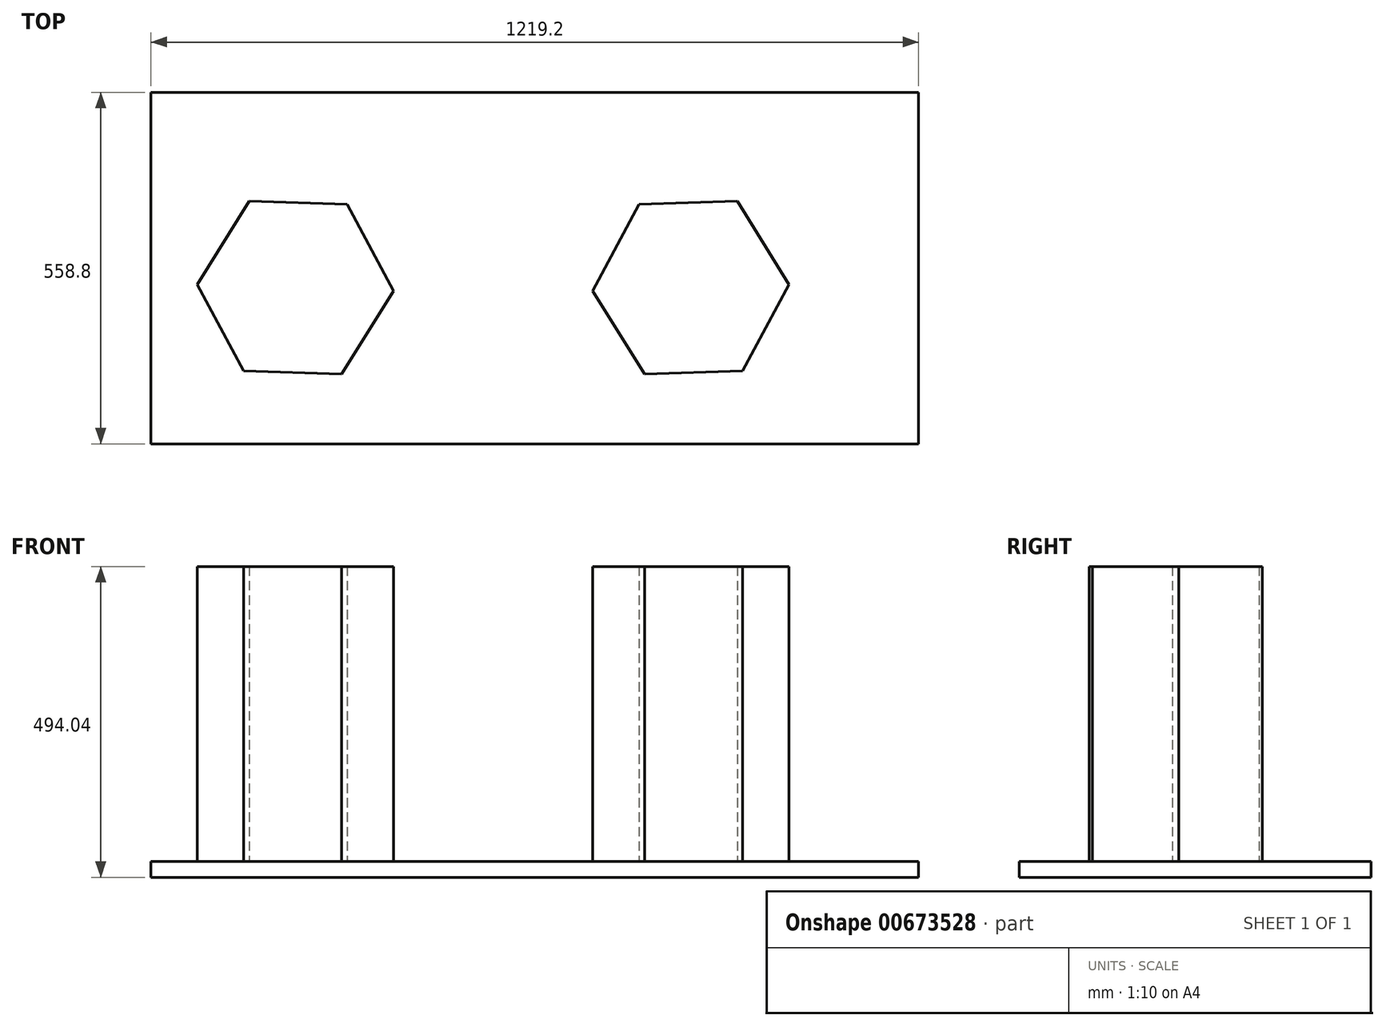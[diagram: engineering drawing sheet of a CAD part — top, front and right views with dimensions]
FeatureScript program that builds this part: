
annotation { "Feature Type Name" : "Feature", "Feature Type Description" : "" }
export const myFeature = defineFeature(function(context is Context, id is Id, definition is map)
    precondition{}
    {
        {
            var Q0;
            Q0=qCreatedBy(makeId("Top.planeOp"),FACE);
            var sketch = newSketch(context, id + "F0", { "sketchPlane" : qUnion([Q0])});
            skLineSegment(sketch, "E0.bottom", {"start": v(0, 0) * mm, "end": v(1219.2, 0) * mm});
            skLineSegment(sketch, "E0.top", {"start": v(0, 558.8) * mm, "end": v(1219.2, 558.8) * mm});
            skLineSegment(sketch, "E0.left", {"start": v(0, 0) * mm, "end": v(0, 558.8) * mm});
            skLineSegment(sketch, "E0.right", {"start": v(1219.2, 0) * mm, "end": v(1219.2, 558.8) * mm});
            skSolve(sketch);
        }
        {
            var Q0;
            Q0 = qSketchRegion(id + "F0", true);
            extrude(context, id + "F1", {"entities" : qUnion([Q0]), "oppositeDirection" : true, "depth" : 25.4 * mm, "offsetDistance" : 25.4 * mm});
        }
        {
            var Q0;
            Q0=makeQuery(id+"F1.opExtrude","CAP_FACE",FACE,{"disambiguationData":[OSD([sQuery(id+"F0.wireOp",EDGE,"E0.bottom"),sQuery(id+"F0.wireOp",EDGE,"E0.top"),sQuery(id+"F0.wireOp",EDGE,"E0.left"),sQuery(id+"F0.wireOp",EDGE,"E0.right")])],"isStart":true});
            var sketch = newSketch(context, id + "F2", { "sketchPlane" : qUnion([Q0])});
            skCircle(sketch, "E1.cCircle", {"center": v(229.23, 248.15) * mm, "radius": 155.97 * mm, "construction": true});
            skLineSegment(sketch, "E1.0", {"start": v(311.48, 380.67) * mm, "end": v(385.11, 243.18) * mm});
            skLineSegment(sketch, "E1.1", {"start": v(385.11, 243.18) * mm, "end": v(302.86, 110.66) * mm});
            skLineSegment(sketch, "E1.2", {"start": v(302.86, 110.66) * mm, "end": v(146.97, 115.64) * mm});
            skLineSegment(sketch, "E1.3", {"start": v(146.97, 115.64) * mm, "end": v(73.34, 253.13) * mm});
            skLineSegment(sketch, "E1.4", {"start": v(73.34, 253.13) * mm, "end": v(155.59, 385.64) * mm});
            skLineSegment(sketch, "E1.5", {"start": v(155.59, 385.64) * mm, "end": v(311.48, 380.67) * mm});
            skLineSegment(sketch, "E2", {"start": v(543.38, 98.5) * mm, "end": v(543.38, 453.78) * mm});
            skLineSegment(sketch, "E3.MirrorCS", {"start": v(701.65, 243.18) * mm, "end": v(783.9, 110.66) * mm});
            skCircle(sketch, "E4.MirrorC", {"center": v(857.53, 248.15) * mm, "radius": 155.97 * mm, "construction": true});
            skLineSegment(sketch, "E5.MirrorCS", {"start": v(783.9, 110.66) * mm, "end": v(939.78, 115.64) * mm});
            skLineSegment(sketch, "E6.MirrorCS", {"start": v(939.78, 115.64) * mm, "end": v(1013.42, 253.13) * mm});
            skLineSegment(sketch, "E7.MirrorCS", {"start": v(1013.42, 253.13) * mm, "end": v(931.17, 385.64) * mm});
            skLineSegment(sketch, "E8.MirrorCS", {"start": v(931.17, 385.64) * mm, "end": v(775.28, 380.67) * mm});
            skLineSegment(sketch, "E9.MirrorCS", {"start": v(775.28, 380.67) * mm, "end": v(701.65, 243.18) * mm});
            skSolve(sketch);
        }
        {
            var Q0;
            Q0=makeQuery(id+"F2.imprint","IMPRINT",FACE,{"disambiguationData":[TD([[makeQuery(id+"F2.imprint","IMPRINT",EDGE,{"derivedFrom":sQuery(id+"F2.wireOp",EDGE,"E1.0")}),-1.0]])]});
            var Q1;
            Q1=makeQuery(id+"F2.imprint","IMPRINT",FACE,{"disambiguationData":[TD([[makeQuery(id+"F2.imprint","IMPRINT",EDGE,{"derivedFrom":sQuery(id+"F2.wireOp",EDGE,"E3.MirrorCS")}),1.0]])]});
            extrude(context, id + "F3", {"entities" : qUnion([Q0, Q1]), "operationType" : NewBodyOperationType.ADD, "depth" : 468.64 * mm, "offsetDistance" : 25.4 * mm});
        }
    });
